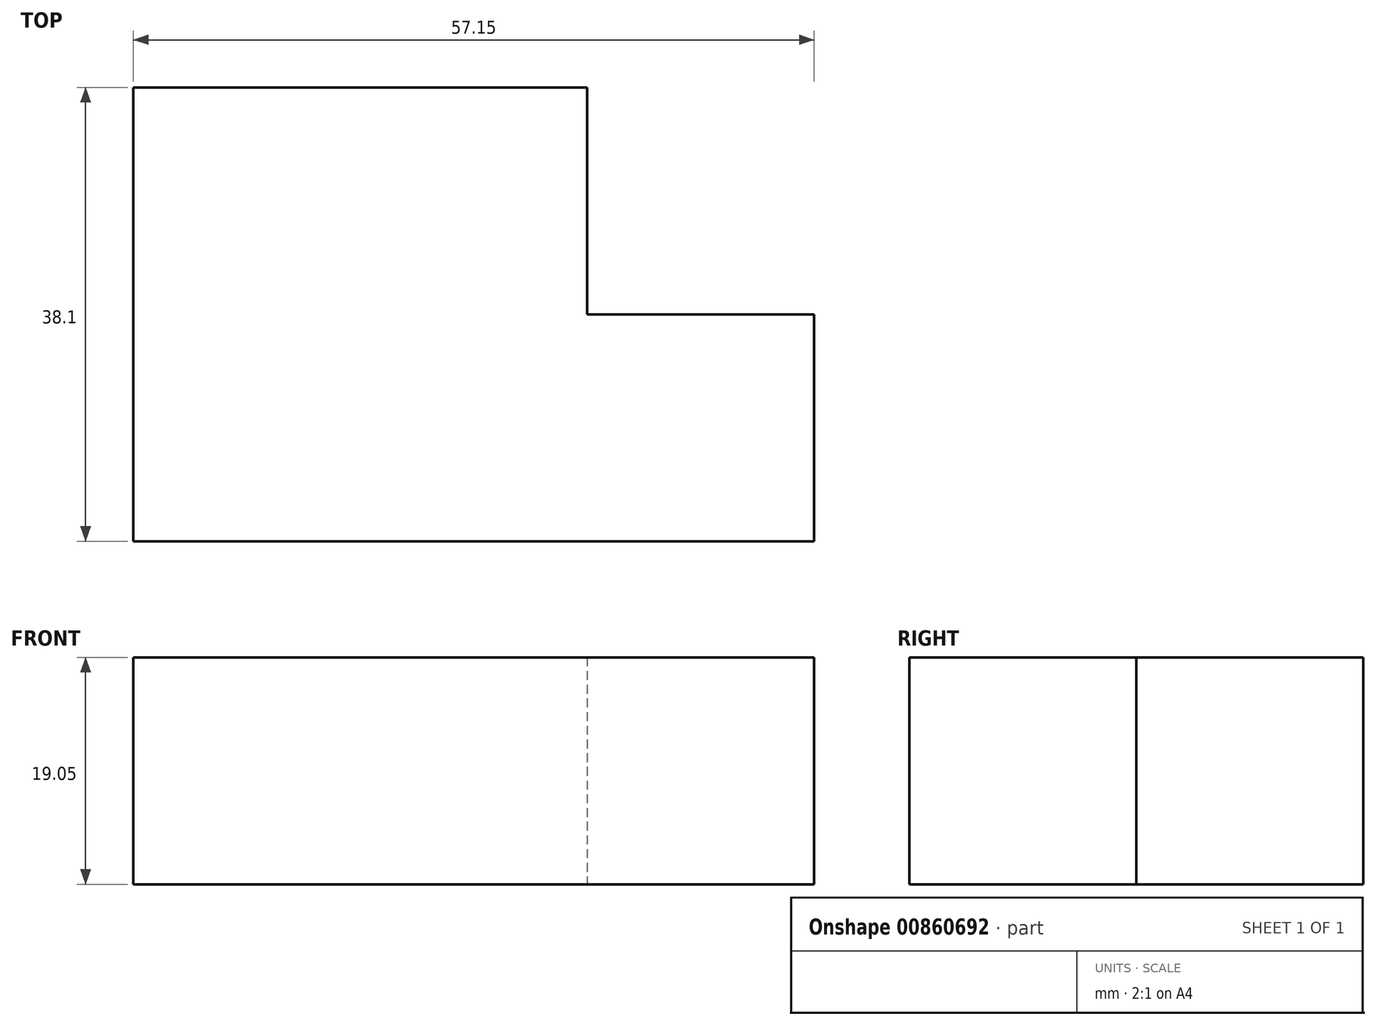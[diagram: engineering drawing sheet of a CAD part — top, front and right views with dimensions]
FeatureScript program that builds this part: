
annotation { "Feature Type Name" : "Feature", "Feature Type Description" : "" }
export const myFeature = defineFeature(function(context is Context, id is Id, definition is map)
    precondition{}
    {
        {
            var Q0;
            Q0=qCreatedBy(makeId("Top.planeOp"),FACE);
            var sketch = newSketch(context, id + "F0", { "sketchPlane" : qUnion([Q0])});
            skLineSegment(sketch, "E0", {"start": v(0, 0) * mm, "end": v(0, -38.1) * mm});
            skLineSegment(sketch, "E1", {"start": v(0, -38.1) * mm, "end": v(57.15, -38.1) * mm});
            skLineSegment(sketch, "E2", {"start": v(57.15, -38.1) * mm, "end": v(57.15, -19.05) * mm});
            skLineSegment(sketch, "E3", {"start": v(57.15, -19.05) * mm, "end": v(38.1, -19.05) * mm});
            skLineSegment(sketch, "E4", {"start": v(38.1, -19.05) * mm, "end": v(38.1, 0) * mm});
            skLineSegment(sketch, "E5", {"start": v(38.1, 0) * mm, "end": v(0, 0) * mm});
            skSolve(sketch);
        }
        {
            var Q0;
            Q0 = qSketchRegion(id + "F0", true);
            extrude(context, id + "F1", {"entities" : qUnion([Q0]), "depth" : 19.05 * mm, "offsetDistance" : 25.4 * mm});
        }
    });
